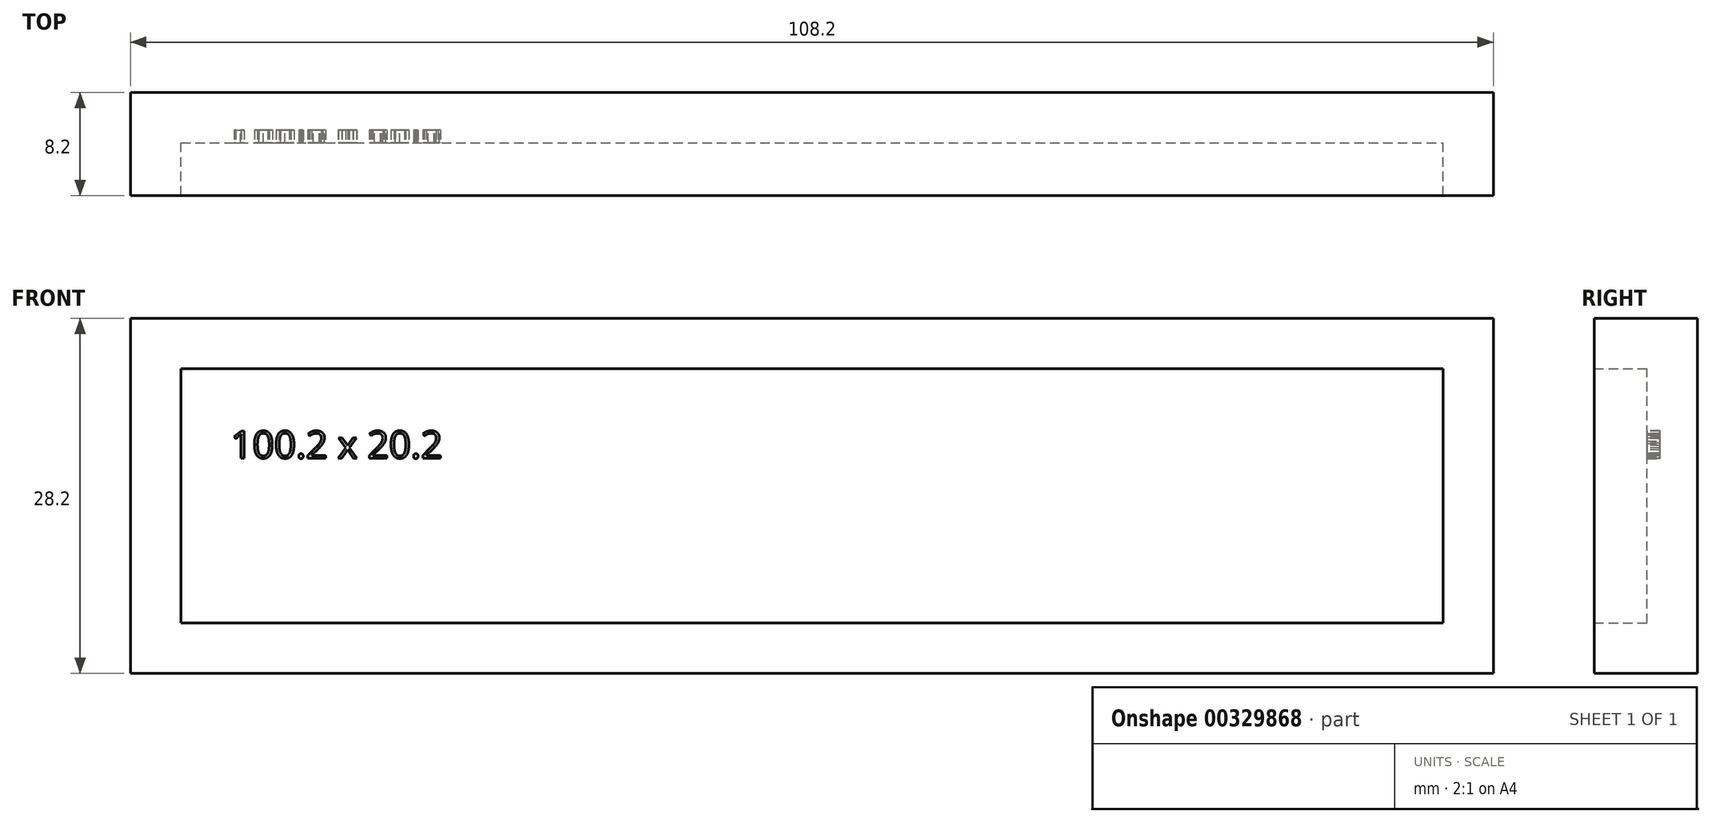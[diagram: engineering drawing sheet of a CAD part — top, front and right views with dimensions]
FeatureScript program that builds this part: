
annotation { "Feature Type Name" : "Feature", "Feature Type Description" : "" }
export const myFeature = defineFeature(function(context is Context, id is Id, definition is map)
    precondition{}
    {
        {
            assignVariable(context, id + "F0", {"name" : "Depth", "anyValue" : 4});
        }
        {
            assignVariable(context, id + "F1", {"name" : "FitGap", "anyValue" : 0.2});
        }
        {
            assignVariable(context, id + "F2", {"name" : "Thickness", "anyValue" : 4});
        }
        {
            var Q0;
            Q0=qCreatedBy(makeId("Front.planeOp"),FACE);
            var sketch = newSketch(context, id + "F3", { "sketchPlane" : qUnion([Q0])});
            skLineSegment(sketch, "E0.bottom", {"start": v(0, 0) * mm, "end": v(108.2, 0) * mm});
            skLineSegment(sketch, "E0.top", {"start": v(0, 28.2) * mm, "end": v(108.2, 28.2) * mm});
            skLineSegment(sketch, "E0.left", {"start": v(0, 0) * mm, "end": v(0, 28.2) * mm});
            skLineSegment(sketch, "E0.right", {"start": v(108.2, 0) * mm, "end": v(108.2, 28.2) * mm});
            skSolve(sketch);
        }
        {
            var Q0;
            Q0=makeQuery(id+"F3.imprint","IMPRINT",FACE,{"disambiguationData":[TD([[makeQuery(id+"F3.imprint","IMPRINT",EDGE,{"derivedFrom":sQuery(id+"F3.wireOp",EDGE,"E0.bottom")}),1.0]])]});
            extrude(context, id + "F4", {"entities" : qUnion([Q0]), "depth" : (getVariable(context, 'Depth') + getVariable(context, 'FitGap') + getVariable(context, 'Thickness')) * mm, "offsetDistance" : 25 * mm});
        }
        {
            var Q0;
            Q0=makeQuery(id+"F4.opExtrude","CAP_FACE",FACE,{"disambiguationData":[OSD([sQuery(id+"F3.wireOp",EDGE,"E0.bottom"),sQuery(id+"F3.wireOp",EDGE,"E0.top"),sQuery(id+"F3.wireOp",EDGE,"E0.left"),sQuery(id+"F3.wireOp",EDGE,"E0.right")])],"isStart":false});
            shell(context, id + "F5", {"entities" : qUnion([Q0]), "thickness" : (getVariable(context, 'Thickness')) * mm});
        }
        {
            var Q0;
            Q0=makeQuery(id+"F5.opShell","OFFSET_FACE",FACE,{"disambiguationData":[OSD([sQuery(id+"F3.wireOp",EDGE,"E0.bottom"),sQuery(id+"F3.wireOp",EDGE,"E0.top"),sQuery(id+"F3.wireOp",EDGE,"E0.left"),sQuery(id+"F3.wireOp",EDGE,"E0.right")])]});
            var sketch = newSketch(context, id + "F6", { "sketchPlane" : qUnion([Q0])});
            skText(sketch, "E1", { "text": "100.2 x 20.2", "fontName": "OpenSans-Regular.ttf"});
            const initialGuessF6  = {"E1": [0.00796, 0.0171, 1, 0, 0.00217]};
            skSetInitialGuess(sketch, initialGuessF6);
            skSolve(sketch);
        }
        {
            var Q0;
            Q0 = qSketchRegion(id + "F6", true);
            extrude(context, id + "F7", {"entities" : qUnion([Q0]), "operationType" : NewBodyOperationType.REMOVE, "oppositeDirection" : true, "depth" : (getVariable(context, 'Thickness') / 4) * mm, "offsetDistance" : 25 * mm});
        }
    });
